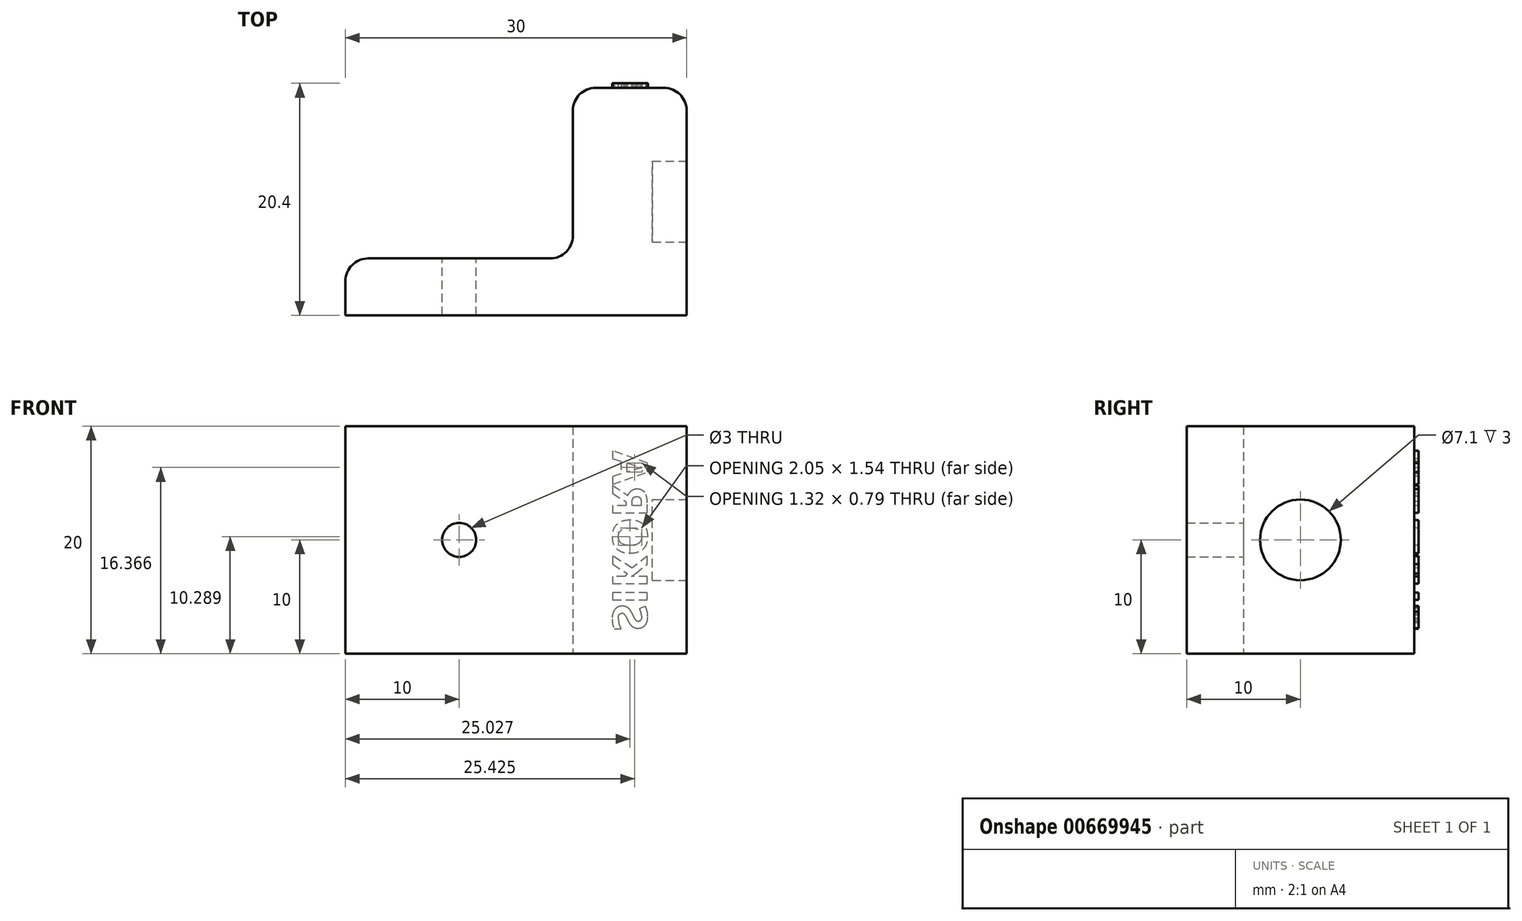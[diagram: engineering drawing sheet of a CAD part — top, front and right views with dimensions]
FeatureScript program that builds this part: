
annotation { "Feature Type Name" : "Feature", "Feature Type Description" : "" }
export const myFeature = defineFeature(function(context is Context, id is Id, definition is map)
    precondition{}
    {
        {
            var Q0;
            Q0=qCreatedBy(makeId("Top.planeOp"),FACE);
            var sketch = newSketch(context, id + "F0", { "sketchPlane" : qUnion([Q0])});
            skLineSegment(sketch, "E0", {"start": v(20, 0) * mm, "end": v(20, 15) * mm});
            skLineSegment(sketch, "E1.0", {"start": v(30, -5) * mm, "end": v(30, 15) * mm});
            skLineSegment(sketch, "E1.1", {"start": v(0, -5) * mm, "end": v(30, -5) * mm});
            skLineSegment(sketch, "E2", {"start": v(20, 15) * mm, "end": v(30, 15) * mm});
            skLineSegment(sketch, "E3", {"start": v(0, 0) * mm, "end": v(0, -5) * mm});
            skLineSegment(sketch, "E4", {"start": v(0, 0) * mm, "end": v(20, 0) * mm});
            skSolve(sketch);
        }
        {
            var Q0;
            Q0=makeQuery(id+"F0.imprint","IMPRINT",FACE,{"disambiguationData":[TD([[makeQuery(id+"F0.imprint","IMPRINT",EDGE,{"derivedFrom":sQuery(id+"F0.wireOp",EDGE,"E0")}),-1.0]])]});
            extrude(context, id + "F1", {"entities" : qUnion([Q0]), "depth" : 20 * mm, "offsetDistance" : 25 * mm});
        }
        {
            var Q0;
            Q0=makeQuery(id+"F1.opExtrude","SWEPT_FACE",FACE,{"disambiguationData":[OSD([sQuery(id+"F0.wireOp",EDGE,"E1.0")])]});
            var sketch = newSketch(context, id + "F2", { "sketchPlane" : qUnion([Q0])});
            skCircle(sketch, "E5", {"center": v(5, 10) * mm, "radius": 3.55 * mm});
            skPoint(sketch, "E5.centerSnap0", {"position": v(5, 20) * mm});
            skPoint(sketch, "E5.centerSnap1", {"position": v(15, 10) * mm});
            skSolve(sketch);
        }
        {
            var Q0;
            Q0=makeQuery(id+"F2.imprint","IMPRINT",FACE,{"disambiguationData":[TD([[makeQuery(id+"F2.imprint","IMPRINT",EDGE,{"derivedFrom":sQuery(id+"F2.wireOp",EDGE,"E5")}),1.0]])]});
            extrude(context, id + "F3", {"entities" : qUnion([Q0]), "operationType" : NewBodyOperationType.REMOVE, "oppositeDirection" : true, "depth" : 3 * mm, "offsetDistance" : 25 * mm});
        }
        {
            var Q0;
            Q0=makeQuery(id+"F1.opExtrude","SWEPT_FACE",FACE,{"disambiguationData":[OSD([sQuery(id+"F0.wireOp",EDGE,"E4")])]});
            var sketch = newSketch(context, id + "F4", { "sketchPlane" : qUnion([Q0])});
            skCircle(sketch, "E6", {"center": v(-10, 10) * mm, "radius": 1.5 * mm});
            skPoint(sketch, "E6.centerSnap0", {"position": v(0, 10) * mm});
            skPoint(sketch, "E6.centerSnap1", {"position": v(-10, 20) * mm});
            skSolve(sketch);
        }
        {
            var Q0;
            Q0=makeQuery(id+"F4.imprint","IMPRINT",FACE,{"disambiguationData":[TD([[makeQuery(id+"F4.imprint","IMPRINT",EDGE,{"derivedFrom":sQuery(id+"F4.wireOp",EDGE,"E6")}),1.0]])]});
            var Q1;
            Q1=sQuery(id+"F4.wireOp",EDGE,"E6");
            extrude(context, id + "F5", {"entities" : qUnion([Q0]), "operationType" : NewBodyOperationType.REMOVE, "surfaceEntities" : qUnion([Q1]), "oppositeDirection" : true, "depth" : 25 * mm, "offsetDistance" : 25 * mm});
        }
        {
            var Q0;
            Q0=makeQuery(id+"F1.opExtrude","SWEPT_EDGE",EDGE,{"disambiguationData":[OSD([sQuery(id+"F0.wireOp",EDGE,"E0"),sQuery(id+"F0.wireOp",EDGE,"E4")])]});
            var Q1;
            Q1=makeQuery(id+"F1.opExtrude","SWEPT_EDGE",EDGE,{"disambiguationData":[OSD([sQuery(id+"F0.wireOp",EDGE,"E3"),sQuery(id+"F0.wireOp",EDGE,"E4")])]});
            var Q2;
            Q2=makeQuery(id+"F1.opExtrude","SWEPT_EDGE",EDGE,{"disambiguationData":[OSD([sQuery(id+"F0.wireOp",EDGE,"E1.0"),sQuery(id+"F0.wireOp",EDGE,"E2")])]});
            var Q3;
            Q3=makeQuery(id+"F1.opExtrude","SWEPT_EDGE",EDGE,{"disambiguationData":[OSD([sQuery(id+"F0.wireOp",EDGE,"E0"),sQuery(id+"F0.wireOp",EDGE,"E2")])]});
            fillet(context, id + "F6", {"entities" : qUnion([Q0, Q1, Q2, Q3]), "radius" : 2 * mm, "tangentPropagation" : true, "allowEdgeOverflow" : false});
        }
        {
            var Q0;
            Q0=makeQuery(id+"F1.opExtrude","SWEPT_FACE",FACE,{"disambiguationData":[OSD([sQuery(id+"F0.wireOp",EDGE,"E2")])]});
            var sketch = newSketch(context, id + "F7", { "sketchPlane" : qUnion([Q0])});
            skText(sketch, "E7", { "text": "SIKORA", "fontName": "OpenSans-Bold.ttf"});
            const initialGuessF7  = {"E7": [-0.0235, 0.002, 0, 1, 0.00307]};
            skSetInitialGuess(sketch, initialGuessF7);
            skSolve(sketch);
        }
        {
            var Q0;
            Q0=qSketchRegion(id+"F7",true);
            extrude(context, id + "F8", {"entities" : qUnion([Q0]), "depth" : .4 * mm, "offsetDistance" : 25 * mm});
        }
    });
